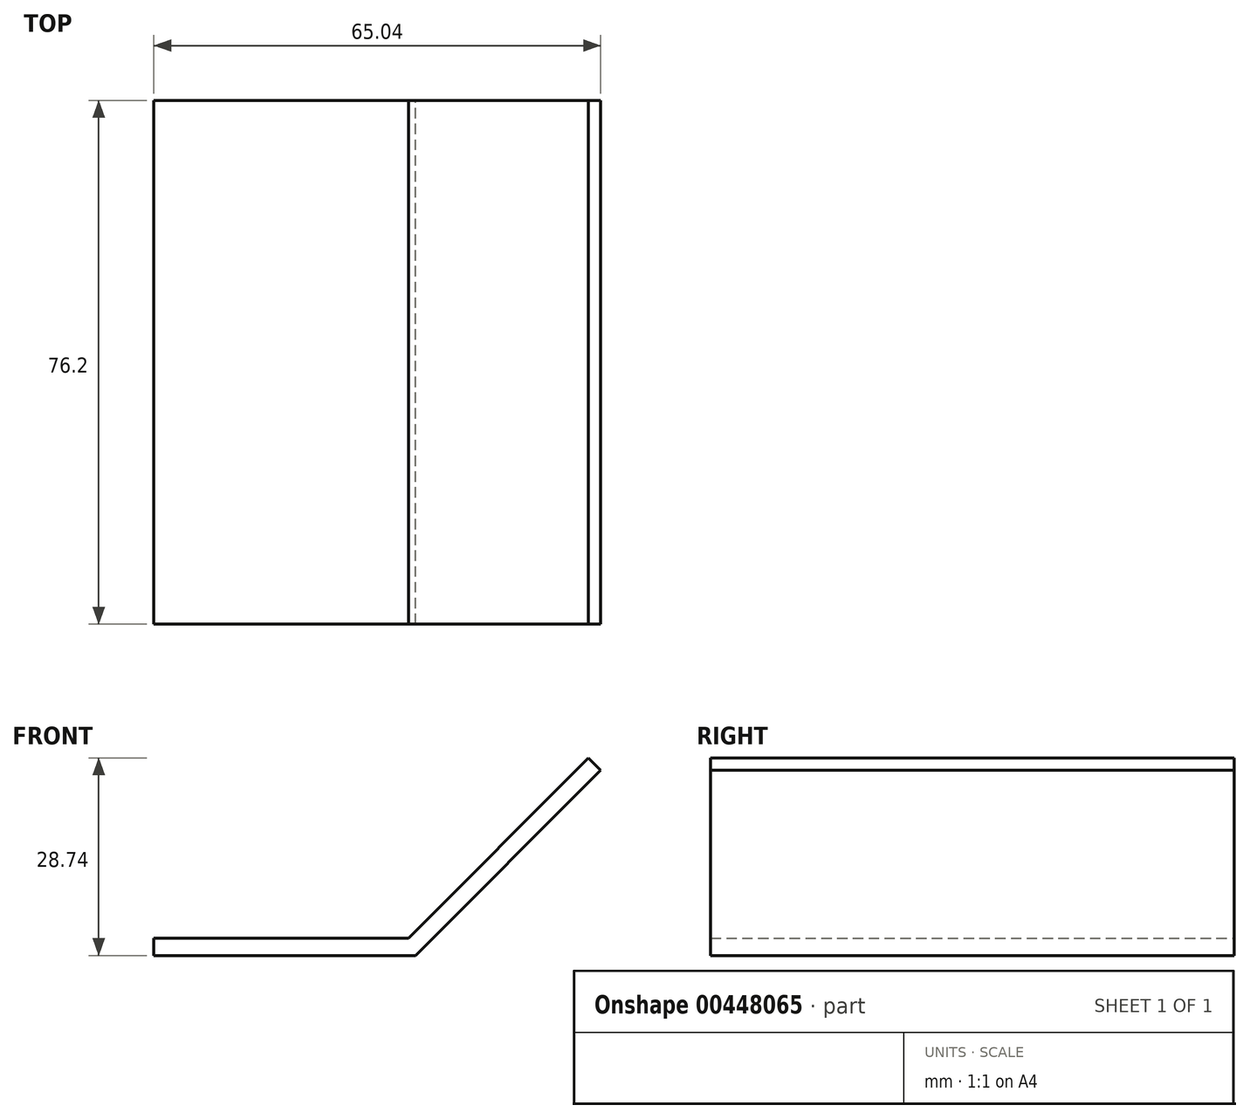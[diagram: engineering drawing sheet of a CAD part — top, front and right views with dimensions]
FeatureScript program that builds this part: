
annotation { "Feature Type Name" : "Feature", "Feature Type Description" : "" }
export const myFeature = defineFeature(function(context is Context, id is Id, definition is map)
    precondition{}
    {
        {
            var Q0;
            Q0=qCreatedBy(makeId("Front.planeOp"),FACE);
            var sketch = newSketch(context, id + "F0", { "sketchPlane" : qUnion([Q0])});
            skLineSegment(sketch, "E0", {"start": v(0, 0) * mm, "end": v(38.1, 0) * mm});
            skLineSegment(sketch, "E1", {"start": v(38.1, 0) * mm, "end": v(65.04, 26.94) * mm});
            skLineSegment(sketch, "E2.0", {"start": v(37.05, 2.54) * mm, "end": v(63.24, 28.74) * mm});
            skLineSegment(sketch, "E2.1", {"start": v(0, 2.54) * mm, "end": v(37.05, 2.54) * mm});
            skLineSegment(sketch, "E3", {"start": v(0, 2.54) * mm, "end": v(0, 0) * mm});
            skLineSegment(sketch, "E4", {"start": v(63.24, 28.74) * mm, "end": v(65.04, 26.94) * mm});
            skSolve(sketch);
        }
        {
            var Q0;
            Q0=makeQuery(id+"F0.imprint","IMPRINT",FACE,{"disambiguationData":[TD([[makeQuery(id+"F0.imprint","IMPRINT",EDGE,{"derivedFrom":sQuery(id+"F0.wireOp",EDGE,"E0")}),1.0]])]});
            extrude(context, id + "F1", {"entities" : qUnion([Q0]), "depth" : 76.2 * mm});
        }
    });
